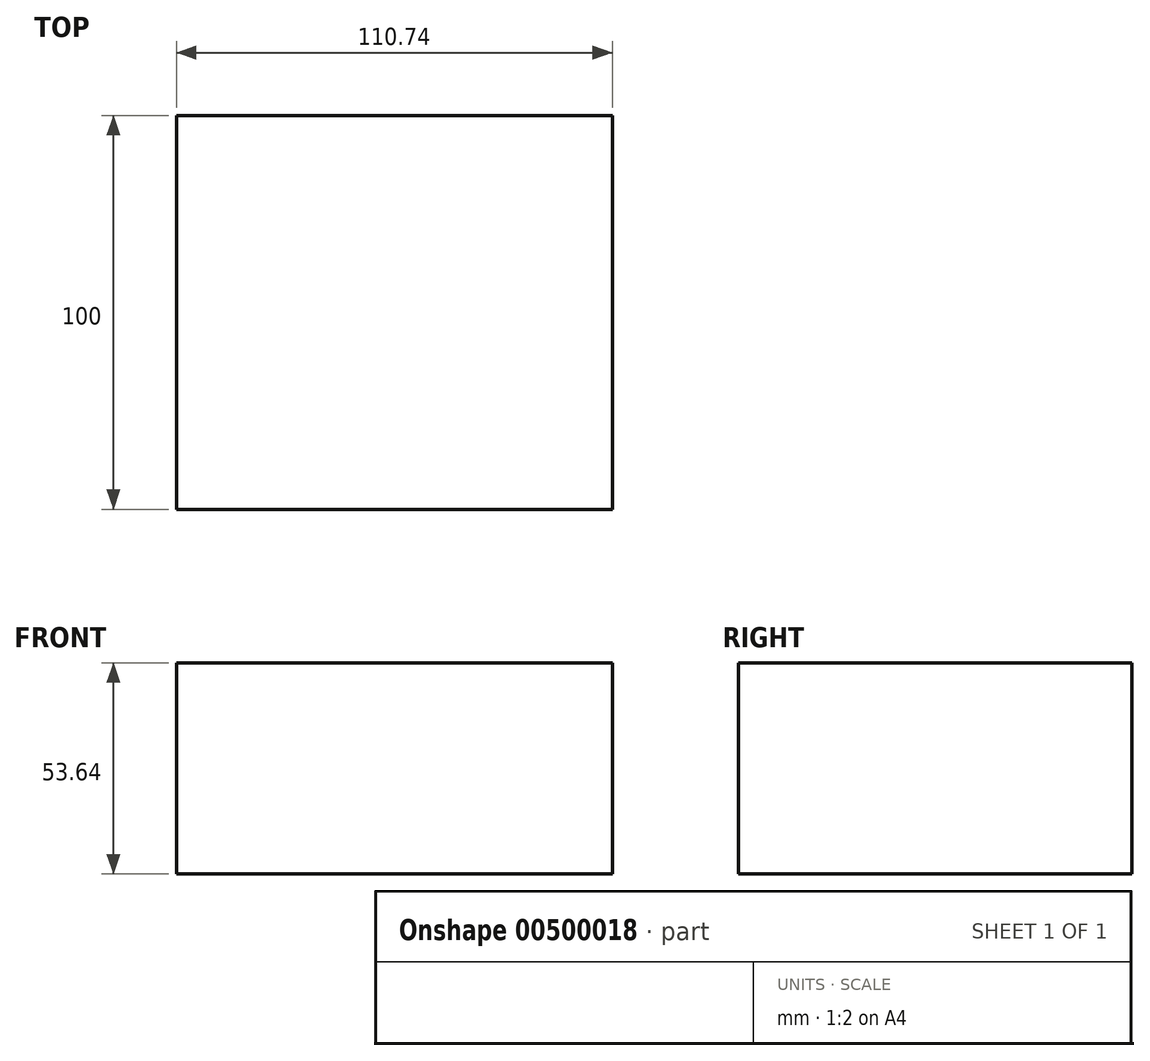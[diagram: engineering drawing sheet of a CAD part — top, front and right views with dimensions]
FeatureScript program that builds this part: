
annotation { "Feature Type Name" : "Feature", "Feature Type Description" : "" }
export const myFeature = defineFeature(function(context is Context, id is Id, definition is map)
    precondition{}
    {
        {
            var Q0;
            Q0=qCreatedBy(makeId("Front.planeOp"),FACE);
            var sketch = newSketch(context, id + "F0", { "sketchPlane" : qUnion([Q0])});
            skLineSegment(sketch, "E0.bottom", {"start": v(-55.37, 26.82) * mm, "end": v(55.37, 26.82) * mm});
            skLineSegment(sketch, "E0.top", {"start": v(-55.37, -26.82) * mm, "end": v(55.37, -26.82) * mm});
            skLineSegment(sketch, "E0.left", {"start": v(-55.37, 26.82) * mm, "end": v(-55.37, -26.82) * mm});
            skLineSegment(sketch, "E0.right", {"start": v(55.37, 26.82) * mm, "end": v(55.37, -26.82) * mm});
            skPoint(sketch, "E0.middle", {"position": v(0, 0) * mm});
            skSolve(sketch);
        }
        {
            var Q0;
            Q0=makeQuery(id+"F0.imprint","IMPRINT",FACE,{"disambiguationData":[TD([[makeQuery(id+"F0.imprint","IMPRINT",EDGE,{"derivedFrom":sQuery(id+"F0.wireOp",EDGE,"E0.bottom")}),-1.0]])]});
            extrude(context, id + "F1", {"entities" : qUnion([Q0]), "endBound" : BoundingType.SYMMETRIC, "depth" : 100 * mm});
        }
    });
